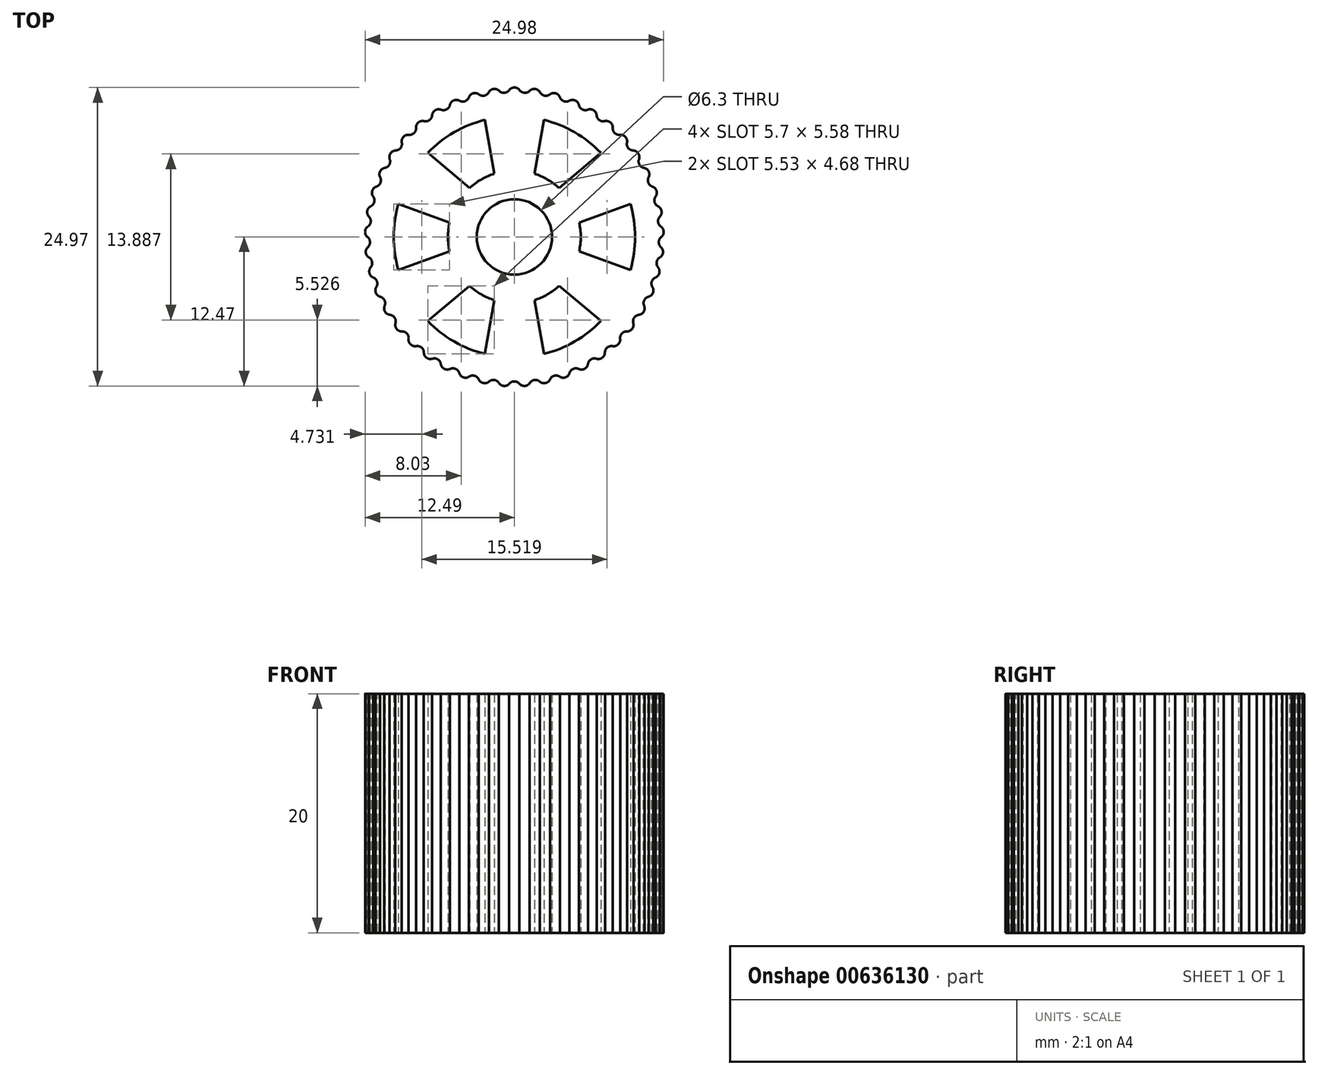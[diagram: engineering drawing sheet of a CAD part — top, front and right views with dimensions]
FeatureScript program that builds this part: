
annotation { "Feature Type Name" : "Feature", "Feature Type Description" : "" }
export const myFeature = defineFeature(function(context is Context, id is Id, definition is map)
    precondition{}
    {
        {
            var Q0;
            Q0=qCreatedBy(makeId("Top.planeOp"),FACE);
            var sketch = newSketch(context, id + "F0", { "sketchPlane" : qUnion([Q0])});
            skCircle(sketch, "E0", {"center": v(0, 0) * mm, "radius": 12.5 * mm});
            skCircle(sketch, "E1", {"center": v(0, 0) * mm, "radius": 3.15 * mm});
            skCircle(sketch, "E2", {"center": v(0, 0) * mm, "radius": 5.55 * mm});
            skCircle(sketch, "E3", {"center": v(0, 0) * mm, "radius": 10.1 * mm});
            skLineSegment(sketch, "E4", {"start": v(-5.42, -1.2) * mm, "end": v(-9.71, -2.76) * mm});
            skLineSegment(sketch, "E5", {"start": v(-5.55, 0) * mm, "end": v(-10.1, 0) * mm, "construction": true});
            skLineSegment(sketch, "E6.MirrorCS", {"start": v(-5.42, 1.2) * mm, "end": v(-9.71, 2.76) * mm});
            skLineSegment(sketch, "E7.1.0", {"start": v(-3.75, -4.1) * mm, "end": v(-7.25, -7.03) * mm});
            skLineSegment(sketch, "E7.1.1", {"start": v(-1.67, -5.3) * mm, "end": v(-2.46, -9.8) * mm});
            skLineSegment(sketch, "E7.2.0", {"start": v(1.67, -5.3) * mm, "end": v(2.46, -9.8) * mm});
            skLineSegment(sketch, "E7.2.1", {"start": v(3.75, -4.1) * mm, "end": v(7.25, -7.03) * mm});
            skLineSegment(sketch, "E7.3.0", {"start": v(5.42, -1.2) * mm, "end": v(9.71, -2.76) * mm});
            skLineSegment(sketch, "E7.3.1", {"start": v(5.42, 1.2) * mm, "end": v(9.71, 2.76) * mm});
            skLineSegment(sketch, "E7.4.0", {"start": v(3.75, 4.1) * mm, "end": v(7.25, 7.03) * mm});
            skLineSegment(sketch, "E7.4.1", {"start": v(1.67, 5.3) * mm, "end": v(2.46, 9.8) * mm});
            skLineSegment(sketch, "E7.5.0", {"start": v(-1.67, 5.3) * mm, "end": v(-2.46, 9.8) * mm});
            skLineSegment(sketch, "E7.5.1", {"start": v(-3.75, 4.1) * mm, "end": v(-7.25, 7.03) * mm});
            skSolve(sketch);
        }
        {
            var Q0;
            Q0=makeQuery(id+"F0.imprint","IMPRINT",FACE,{"disambiguationData":[TD([[makeQuery(id+"F0.imprint","IMPRINT",EDGE,{"derivedFrom":sQuery(id+"F0.wireOp",EDGE,"E0")}),1.0]])]});
            var Q1;
            {var subQ0=sQuery(id+"F0.wireOp",EDGE,"E6.MirrorCS");Q1=makeQuery(id+"F0.imprint","IMPRINT",FACE,{"disambiguationData":[TD([[makeQuery(id+"F0.imprint","IMPRINT",EDGE,{"derivedFrom":subQ0}),-1.0]])]});}
            var Q2;
            {var subQ0=sQuery(id+"F0.wireOp",EDGE,"E7.4.1");Q2=makeQuery(id+"F0.imprint","IMPRINT",FACE,{"disambiguationData":[TD([[makeQuery(id+"F0.imprint","IMPRINT",EDGE,{"derivedFrom":subQ0}),1.0]])]});}
            var Q3;
            {var subQ0=sQuery(id+"F0.wireOp",EDGE,"E7.3.1");Q3=makeQuery(id+"F0.imprint","IMPRINT",FACE,{"disambiguationData":[TD([[makeQuery(id+"F0.imprint","IMPRINT",EDGE,{"derivedFrom":subQ0}),1.0]])]});}
            var Q4;
            {var subQ0=sQuery(id+"F0.wireOp",EDGE,"E7.2.1");Q4=makeQuery(id+"F0.imprint","IMPRINT",FACE,{"disambiguationData":[TD([[makeQuery(id+"F0.imprint","IMPRINT",EDGE,{"derivedFrom":subQ0}),1.0]])]});}
            var Q5;
            {var subQ0=sQuery(id+"F0.wireOp",EDGE,"E7.1.1");Q5=makeQuery(id+"F0.imprint","IMPRINT",FACE,{"disambiguationData":[TD([[makeQuery(id+"F0.imprint","IMPRINT",EDGE,{"derivedFrom":subQ0}),1.0]])]});}
            var Q6;
            {var subQ0=sQuery(id+"F0.wireOp",EDGE,"E4");Q6=makeQuery(id+"F0.imprint","IMPRINT",FACE,{"disambiguationData":[TD([[makeQuery(id+"F0.imprint","IMPRINT",EDGE,{"derivedFrom":subQ0}),1.0]])]});}
            var Q7;
            Q7=makeQuery(id+"F0.imprint","IMPRINT",FACE,{"disambiguationData":[TD([[makeQuery(id+"F0.imprint","IMPRINT",EDGE,{"derivedFrom":sQuery(id+"F0.wireOp",EDGE,"E1")}),-1.0]])]});
            extrude(context, id + "F1", {"entities" : qUnion([Q0, Q1, Q2, Q3, Q4, Q5, Q6, Q7]), "depth" : 20 * mm, "offsetDistance" : 25 * mm});
        }
        {
            var Q0;
            Q0=makeQuery(id+"F1.opExtrude","CAP_FACE",FACE,{"disambiguationData":[OSD([sQuery(id+"F0.wireOp",EDGE,"E0"),sQuery(id+"F0.wireOp",EDGE,"E1"),sQuery(id+"F0.wireOp",EDGE,"E2"),sQuery(id+"F0.wireOp",EDGE,"E3"),sQuery(id+"F0.wireOp",EDGE,"E4"),sQuery(id+"F0.wireOp",EDGE,"E6.MirrorCS"),sQuery(id+"F0.wireOp",EDGE,"E7.1.0"),sQuery(id+"F0.wireOp",EDGE,"E7.1.1"),sQuery(id+"F0.wireOp",EDGE,"E7.2.0"),sQuery(id+"F0.wireOp",EDGE,"E7.2.1"),sQuery(id+"F0.wireOp",EDGE,"E7.3.0"),sQuery(id+"F0.wireOp",EDGE,"E7.3.1"),sQuery(id+"F0.wireOp",EDGE,"E7.4.0"),sQuery(id+"F0.wireOp",EDGE,"E7.4.1"),sQuery(id+"F0.wireOp",EDGE,"E7.5.0"),sQuery(id+"F0.wireOp",EDGE,"E7.5.1")])],"isStart":false});
            var sketch = newSketch(context, id + "F2", { "sketchPlane" : qUnion([Q0])});
            skCircle(sketch, "E8", {"center": v(0, 0) * mm, "radius": 12.3 * mm});
            skArc(sketch, "E9", {"start": v(0.43, 12.3) * mm, "mid": v(0, 12.5) * mm, "end": v(-0.43, 12.3) * mm});
            skArc(sketch, "E10", {"start": v(0.43, 12.3) * mm, "mid": v(0.84, 12.06) * mm, "end": v(1.29, 12.23) * mm});
            skLineSegment(sketch, "E11", {"start": v(-0.43, 12.3) * mm, "end": v(0.43, 12.3) * mm, "construction": true});
            skLineSegment(sketch, "E12", {"start": v(0.43, 12.3) * mm, "end": v(1.29, 12.23) * mm, "construction": true});
            skArc(sketch, "E13.1.0", {"start": v(-1.29, 12.23) * mm, "mid": v(-1.74, 12.38) * mm, "end": v(-2.14, 12.11) * mm});
            skArc(sketch, "E13.1.1", {"start": v(-1.29, 12.23) * mm, "mid": v(-0.84, 12.06) * mm, "end": v(-0.43, 12.3) * mm});
            skArc(sketch, "E13.2.0", {"start": v(-2.98, 11.93) * mm, "mid": v(-3.45, 12.02) * mm, "end": v(-3.8, 11.7) * mm});
            skArc(sketch, "E13.2.1", {"start": v(-2.98, 11.93) * mm, "mid": v(-2.51, 11.82) * mm, "end": v(-2.14, 12.11) * mm});
            skArc(sketch, "E13.3.0", {"start": v(-4.6, 11.4) * mm, "mid": v(-5.08, 11.42) * mm, "end": v(-5.4, 11.06) * mm});
            skArc(sketch, "E13.3.1", {"start": v(-4.6, 11.4) * mm, "mid": v(-4.13, 11.36) * mm, "end": v(-3.8, 11.7) * mm});
            skArc(sketch, "E13.4.0", {"start": v(-6.15, 10.65) * mm, "mid": v(-6.62, 10.6) * mm, "end": v(-6.88, 10.2) * mm});
            skArc(sketch, "E13.4.1", {"start": v(-6.15, 10.65) * mm, "mid": v(-5.67, 10.67) * mm, "end": v(-5.4, 11.06) * mm});
            skArc(sketch, "E13.5.0", {"start": v(-7.57, 9.7) * mm, "mid": v(-8.03, 9.58) * mm, "end": v(-8.23, 9.14) * mm});
            skArc(sketch, "E13.5.1", {"start": v(-7.57, 9.7) * mm, "mid": v(-7.1, 9.78) * mm, "end": v(-6.88, 10.2) * mm});
            skArc(sketch, "E13.6.0", {"start": v(-8.85, 8.54) * mm, "mid": v(-9.29, 8.36) * mm, "end": v(-9.42, 7.9) * mm});
            skArc(sketch, "E13.6.1", {"start": v(-8.85, 8.54) * mm, "mid": v(-8.4, 8.7) * mm, "end": v(-8.23, 9.14) * mm});
            skArc(sketch, "E13.7.0", {"start": v(-9.95, 7.23) * mm, "mid": v(-10.36, 6.99) * mm, "end": v(-10.43, 6.52) * mm});
            skArc(sketch, "E13.7.1", {"start": v(-9.95, 7.23) * mm, "mid": v(-9.52, 7.44) * mm, "end": v(-9.42, 7.9) * mm});
            skArc(sketch, "E13.8.0", {"start": v(-10.86, 5.77) * mm, "mid": v(-11.23, 5.48) * mm, "end": v(-11.24, 5) * mm});
            skArc(sketch, "E13.8.1", {"start": v(-10.86, 5.77) * mm, "mid": v(-10.47, 6.04) * mm, "end": v(-10.43, 6.52) * mm});
            skArc(sketch, "E13.9.0", {"start": v(-11.56, 4.2) * mm, "mid": v(-11.89, 3.86) * mm, "end": v(-11.82, 3.4) * mm});
            skArc(sketch, "E13.9.1", {"start": v(-11.56, 4.2) * mm, "mid": v(-11.2, 4.53) * mm, "end": v(-11.24, 5) * mm});
            skArc(sketch, "E13.10.0", {"start": v(-12.03, 2.56) * mm, "mid": v(-12.31, 2.17) * mm, "end": v(-12.18, 1.71) * mm});
            skArc(sketch, "E13.10.1", {"start": v(-12.03, 2.56) * mm, "mid": v(-11.73, 2.92) * mm, "end": v(-11.82, 3.4) * mm});
            skArc(sketch, "E13.11.0", {"start": v(-12.27, 0.86) * mm, "mid": v(-12.5, 0.44) * mm, "end": v(-12.3, 0) * mm});
            skArc(sketch, "E13.11.1", {"start": v(-12.27, 0.86) * mm, "mid": v(-12.02, 1.26) * mm, "end": v(-12.18, 1.71) * mm});
            skArc(sketch, "E13.12.0", {"start": v(-12.27, -0.86) * mm, "mid": v(-12.43, -1.3) * mm, "end": v(-12.18, -1.71) * mm});
            skArc(sketch, "E13.12.1", {"start": v(-12.27, -0.86) * mm, "mid": v(-12.08, -0.42) * mm, "end": v(-12.3, 0) * mm});
            skArc(sketch, "E13.13.0", {"start": v(-12.03, -2.56) * mm, "mid": v(-12.13, -3.02) * mm, "end": v(-11.82, -3.4) * mm});
            skArc(sketch, "E13.13.1", {"start": v(-12.03, -2.56) * mm, "mid": v(-11.9, -2.1) * mm, "end": v(-12.18, -1.71) * mm});
            skArc(sketch, "E13.14.0", {"start": v(-11.56, -4.2) * mm, "mid": v(-11.59, -4.68) * mm, "end": v(-11.24, -5) * mm});
            skArc(sketch, "E13.14.1", {"start": v(-11.56, -4.2) * mm, "mid": v(-11.5, -3.73) * mm, "end": v(-11.82, -3.4) * mm});
            skArc(sketch, "E13.15.0", {"start": v(-10.86, -5.77) * mm, "mid": v(-10.83, -6.25) * mm, "end": v(-10.43, -6.52) * mm});
            skArc(sketch, "E13.15.1", {"start": v(-10.86, -5.77) * mm, "mid": v(-10.86, -5.3) * mm, "end": v(-11.24, -5) * mm});
            skArc(sketch, "E13.16.0", {"start": v(-9.95, -7.23) * mm, "mid": v(-9.85, -7.7) * mm, "end": v(-9.42, -7.9) * mm});
            skArc(sketch, "E13.16.1", {"start": v(-9.95, -7.23) * mm, "mid": v(-10.02, -6.76) * mm, "end": v(-10.43, -6.52) * mm});
            skArc(sketch, "E13.17.0", {"start": v(-8.85, -8.54) * mm, "mid": v(-8.68, -9) * mm, "end": v(-8.23, -9.14) * mm});
            skArc(sketch, "E13.17.1", {"start": v(-8.85, -8.54) * mm, "mid": v(-8.98, -8.09) * mm, "end": v(-9.42, -7.9) * mm});
            skArc(sketch, "E13.18.0", {"start": v(-7.57, -9.7) * mm, "mid": v(-7.35, -10.11) * mm, "end": v(-6.88, -10.2) * mm});
            skArc(sketch, "E13.18.1", {"start": v(-7.57, -9.7) * mm, "mid": v(-7.77, -9.26) * mm, "end": v(-8.23, -9.14) * mm});
            skArc(sketch, "E13.19.0", {"start": v(-6.15, -10.65) * mm, "mid": v(-5.87, -11.04) * mm, "end": v(-5.4, -11.06) * mm});
            skArc(sketch, "E13.19.1", {"start": v(-6.15, -10.65) * mm, "mid": v(-6.4, -10.25) * mm, "end": v(-6.88, -10.2) * mm});
            skArc(sketch, "E13.20.0", {"start": v(-4.6, -11.4) * mm, "mid": v(-4.28, -11.75) * mm, "end": v(-3.8, -11.7) * mm});
            skArc(sketch, "E13.20.1", {"start": v(-4.6, -11.4) * mm, "mid": v(-4.92, -11.04) * mm, "end": v(-5.4, -11.06) * mm});
            skArc(sketch, "E13.21.0", {"start": v(-2.98, -11.93) * mm, "mid": v(-2.6, -12.23) * mm, "end": v(-2.14, -12.11) * mm});
            skArc(sketch, "E13.21.1", {"start": v(-2.98, -11.93) * mm, "mid": v(-3.33, -11.62) * mm, "end": v(-3.8, -11.7) * mm});
            skArc(sketch, "E13.22.0", {"start": v(-1.29, -12.23) * mm, "mid": v(-0.87, -12.47) * mm, "end": v(-0.43, -12.3) * mm});
            skArc(sketch, "E13.22.1", {"start": v(-1.29, -12.23) * mm, "mid": v(-1.68, -11.97) * mm, "end": v(-2.14, -12.11) * mm});
            skArc(sketch, "E13.23.0", {"start": v(0.43, -12.3) * mm, "mid": v(0.87, -12.47) * mm, "end": v(1.29, -12.23) * mm});
            skArc(sketch, "E13.23.1", {"start": v(0.43, -12.3) * mm, "mid": v(0, -12.09) * mm, "end": v(-0.43, -12.3) * mm});
            skArc(sketch, "E13.24.0", {"start": v(2.14, -12.11) * mm, "mid": v(2.6, -12.23) * mm, "end": v(2.98, -11.93) * mm});
            skArc(sketch, "E13.24.1", {"start": v(2.14, -12.11) * mm, "mid": v(1.68, -11.97) * mm, "end": v(1.29, -12.23) * mm});
            skArc(sketch, "E13.25.0", {"start": v(3.8, -11.7) * mm, "mid": v(4.28, -11.75) * mm, "end": v(4.6, -11.4) * mm});
            skArc(sketch, "E13.25.1", {"start": v(3.8, -11.7) * mm, "mid": v(3.33, -11.62) * mm, "end": v(2.98, -11.93) * mm});
            skArc(sketch, "E13.26.0", {"start": v(5.4, -11.06) * mm, "mid": v(5.87, -11.04) * mm, "end": v(6.15, -10.65) * mm});
            skArc(sketch, "E13.26.1", {"start": v(5.4, -11.06) * mm, "mid": v(4.92, -11.04) * mm, "end": v(4.6, -11.4) * mm});
            skArc(sketch, "E13.27.0", {"start": v(6.88, -10.2) * mm, "mid": v(7.35, -10.11) * mm, "end": v(7.57, -9.7) * mm});
            skArc(sketch, "E13.27.1", {"start": v(6.88, -10.2) * mm, "mid": v(6.4, -10.25) * mm, "end": v(6.15, -10.65) * mm});
            skArc(sketch, "E13.28.0", {"start": v(8.23, -9.14) * mm, "mid": v(8.68, -9) * mm, "end": v(8.85, -8.54) * mm});
            skArc(sketch, "E13.28.1", {"start": v(8.23, -9.14) * mm, "mid": v(7.77, -9.26) * mm, "end": v(7.57, -9.7) * mm});
            skArc(sketch, "E13.29.0", {"start": v(9.42, -7.9) * mm, "mid": v(9.85, -7.7) * mm, "end": v(9.95, -7.23) * mm});
            skArc(sketch, "E13.29.1", {"start": v(9.42, -7.9) * mm, "mid": v(8.98, -8.09) * mm, "end": v(8.85, -8.54) * mm});
            skArc(sketch, "E13.30.0", {"start": v(10.43, -6.52) * mm, "mid": v(10.83, -6.25) * mm, "end": v(10.86, -5.77) * mm});
            skArc(sketch, "E13.30.1", {"start": v(10.43, -6.52) * mm, "mid": v(10.02, -6.76) * mm, "end": v(9.95, -7.23) * mm});
            skArc(sketch, "E13.31.0", {"start": v(11.24, -5) * mm, "mid": v(11.59, -4.68) * mm, "end": v(11.56, -4.2) * mm});
            skArc(sketch, "E13.31.1", {"start": v(11.24, -5) * mm, "mid": v(10.86, -5.3) * mm, "end": v(10.86, -5.77) * mm});
            skArc(sketch, "E13.32.0", {"start": v(11.82, -3.4) * mm, "mid": v(12.13, -3.02) * mm, "end": v(12.03, -2.56) * mm});
            skArc(sketch, "E13.32.1", {"start": v(11.82, -3.4) * mm, "mid": v(11.5, -3.73) * mm, "end": v(11.56, -4.2) * mm});
            skArc(sketch, "E13.33.0", {"start": v(12.18, -1.71) * mm, "mid": v(12.43, -1.3) * mm, "end": v(12.27, -0.86) * mm});
            skArc(sketch, "E13.33.1", {"start": v(12.18, -1.71) * mm, "mid": v(11.9, -2.1) * mm, "end": v(12.03, -2.56) * mm});
            skArc(sketch, "E13.34.0", {"start": v(12.3, 0) * mm, "mid": v(12.5, 0.44) * mm, "end": v(12.27, 0.86) * mm});
            skArc(sketch, "E13.34.1", {"start": v(12.3, 0) * mm, "mid": v(12.08, -0.42) * mm, "end": v(12.27, -0.86) * mm});
            skArc(sketch, "E13.35.0", {"start": v(12.18, 1.71) * mm, "mid": v(12.31, 2.17) * mm, "end": v(12.03, 2.56) * mm});
            skArc(sketch, "E13.35.1", {"start": v(12.18, 1.71) * mm, "mid": v(12.02, 1.26) * mm, "end": v(12.27, 0.86) * mm});
            skArc(sketch, "E13.36.0", {"start": v(11.82, 3.4) * mm, "mid": v(11.89, 3.86) * mm, "end": v(11.56, 4.2) * mm});
            skArc(sketch, "E13.36.1", {"start": v(11.82, 3.4) * mm, "mid": v(11.73, 2.92) * mm, "end": v(12.03, 2.56) * mm});
            skArc(sketch, "E13.37.0", {"start": v(11.24, 5) * mm, "mid": v(11.23, 5.48) * mm, "end": v(10.86, 5.77) * mm});
            skArc(sketch, "E13.37.1", {"start": v(11.24, 5) * mm, "mid": v(11.2, 4.53) * mm, "end": v(11.56, 4.2) * mm});
            skArc(sketch, "E13.38.0", {"start": v(10.43, 6.52) * mm, "mid": v(10.36, 6.99) * mm, "end": v(9.95, 7.23) * mm});
            skArc(sketch, "E13.38.1", {"start": v(10.43, 6.52) * mm, "mid": v(10.47, 6.04) * mm, "end": v(10.86, 5.77) * mm});
            skArc(sketch, "E13.39.0", {"start": v(9.42, 7.9) * mm, "mid": v(9.29, 8.36) * mm, "end": v(8.85, 8.54) * mm});
            skArc(sketch, "E13.39.1", {"start": v(9.42, 7.9) * mm, "mid": v(9.52, 7.44) * mm, "end": v(9.95, 7.23) * mm});
            skArc(sketch, "E13.40.0", {"start": v(8.23, 9.14) * mm, "mid": v(8.03, 9.58) * mm, "end": v(7.57, 9.7) * mm});
            skArc(sketch, "E13.40.1", {"start": v(8.23, 9.14) * mm, "mid": v(8.4, 8.7) * mm, "end": v(8.85, 8.54) * mm});
            skArc(sketch, "E13.41.0", {"start": v(6.88, 10.2) * mm, "mid": v(6.62, 10.6) * mm, "end": v(6.15, 10.65) * mm});
            skArc(sketch, "E13.41.1", {"start": v(6.88, 10.2) * mm, "mid": v(7.1, 9.78) * mm, "end": v(7.57, 9.7) * mm});
            skArc(sketch, "E13.42.0", {"start": v(5.4, 11.06) * mm, "mid": v(5.08, 11.42) * mm, "end": v(4.6, 11.4) * mm});
            skArc(sketch, "E13.42.1", {"start": v(5.4, 11.06) * mm, "mid": v(5.67, 10.67) * mm, "end": v(6.15, 10.65) * mm});
            skArc(sketch, "E13.43.0", {"start": v(3.8, 11.7) * mm, "mid": v(3.45, 12.02) * mm, "end": v(2.98, 11.93) * mm});
            skArc(sketch, "E13.43.1", {"start": v(3.8, 11.7) * mm, "mid": v(4.13, 11.36) * mm, "end": v(4.6, 11.4) * mm});
            skArc(sketch, "E13.44.0", {"start": v(2.14, 12.11) * mm, "mid": v(1.74, 12.38) * mm, "end": v(1.29, 12.23) * mm});
            skArc(sketch, "E13.44.1", {"start": v(2.14, 12.11) * mm, "mid": v(2.51, 11.82) * mm, "end": v(2.98, 11.93) * mm});
            skSolve(sketch);
        }
        {
            var Q0;
            {var subQ37=sQuery(id+"F2.wireOp",EDGE,"E10");Q0=makeQuery(id+"F2.imprint","IMPRINT",FACE,{"disambiguationData":[TD([[makeQuery(id+"F2.imprint","IMPRINT",EDGE,{"derivedFrom":subQ37}),-1.0]])]});}
            var Q1;
            {var subQ0=sQuery(id+"F2.wireOp",EDGE,"E13.22.0");var subQ1=sQuery(id+"F2.wireOp",EDGE,"E8");var subQ4=makeQuery(id+"F2.imprint","INTERSECT",VERTEX,{"derivedFrom":[subQ1,subQ0]});Q1=makeQuery(id+"F2.imprint","IMPRINT",FACE,{"disambiguationData":[TD([[makeQuery(id+"F2.imprint","IMPRINT",EDGE,{"disambiguationData":[TD([[subQ4,1.0]])],"derivedFrom":subQ1}),-1.0]])]});}
            var Q2;
            {var subQ0=sQuery(id+"F2.wireOp",EDGE,"E13.23.0");var subQ1=sQuery(id+"F2.wireOp",EDGE,"E8");var subQ4=makeQuery(id+"F2.imprint","INTERSECT",VERTEX,{"derivedFrom":[subQ1,subQ0]});Q2=makeQuery(id+"F2.imprint","IMPRINT",FACE,{"disambiguationData":[TD([[makeQuery(id+"F2.imprint","IMPRINT",EDGE,{"disambiguationData":[TD([[subQ4,1.0]])],"derivedFrom":subQ1}),-1.0]])]});}
            var Q3;
            {var subQ0=sQuery(id+"F2.wireOp",EDGE,"E13.24.0");var subQ1=sQuery(id+"F2.wireOp",EDGE,"E8");var subQ4=makeQuery(id+"F2.imprint","INTERSECT",VERTEX,{"derivedFrom":[subQ1,subQ0]});Q3=makeQuery(id+"F2.imprint","IMPRINT",FACE,{"disambiguationData":[TD([[makeQuery(id+"F2.imprint","IMPRINT",EDGE,{"disambiguationData":[TD([[subQ4,1.0]])],"derivedFrom":subQ1}),-1.0]])]});}
            var Q4;
            {var subQ0=sQuery(id+"F2.wireOp",EDGE,"E13.25.0");var subQ1=sQuery(id+"F2.wireOp",EDGE,"E8");var subQ4=makeQuery(id+"F2.imprint","INTERSECT",VERTEX,{"derivedFrom":[subQ1,subQ0]});Q4=makeQuery(id+"F2.imprint","IMPRINT",FACE,{"disambiguationData":[TD([[makeQuery(id+"F2.imprint","IMPRINT",EDGE,{"disambiguationData":[TD([[subQ4,1.0]])],"derivedFrom":subQ1}),-1.0]])]});}
            var Q5;
            {var subQ0=sQuery(id+"F2.wireOp",EDGE,"E13.26.0");var subQ1=sQuery(id+"F2.wireOp",EDGE,"E8");var subQ4=makeQuery(id+"F2.imprint","INTERSECT",VERTEX,{"derivedFrom":[subQ1,subQ0]});Q5=makeQuery(id+"F2.imprint","IMPRINT",FACE,{"disambiguationData":[TD([[makeQuery(id+"F2.imprint","IMPRINT",EDGE,{"disambiguationData":[TD([[subQ4,1.0]])],"derivedFrom":subQ1}),-1.0]])]});}
            var Q6;
            {var subQ0=sQuery(id+"F2.wireOp",EDGE,"E13.27.0");var subQ1=sQuery(id+"F2.wireOp",EDGE,"E8");var subQ4=makeQuery(id+"F2.imprint","INTERSECT",VERTEX,{"derivedFrom":[subQ1,subQ0]});Q6=makeQuery(id+"F2.imprint","IMPRINT",FACE,{"disambiguationData":[TD([[makeQuery(id+"F2.imprint","IMPRINT",EDGE,{"disambiguationData":[TD([[subQ4,1.0]])],"derivedFrom":subQ1}),-1.0]])]});}
            var Q7;
            {var subQ0=sQuery(id+"F2.wireOp",EDGE,"E13.28.0");var subQ1=sQuery(id+"F2.wireOp",EDGE,"E8");var subQ4=makeQuery(id+"F2.imprint","INTERSECT",VERTEX,{"derivedFrom":[subQ1,subQ0]});Q7=makeQuery(id+"F2.imprint","IMPRINT",FACE,{"disambiguationData":[TD([[makeQuery(id+"F2.imprint","IMPRINT",EDGE,{"disambiguationData":[TD([[subQ4,1.0]])],"derivedFrom":subQ1}),-1.0]])]});}
            var Q8;
            {var subQ0=sQuery(id+"F2.wireOp",EDGE,"E13.29.0");var subQ1=sQuery(id+"F2.wireOp",EDGE,"E8");var subQ4=makeQuery(id+"F2.imprint","INTERSECT",VERTEX,{"derivedFrom":[subQ1,subQ0]});Q8=makeQuery(id+"F2.imprint","IMPRINT",FACE,{"disambiguationData":[TD([[makeQuery(id+"F2.imprint","IMPRINT",EDGE,{"disambiguationData":[TD([[subQ4,1.0]])],"derivedFrom":subQ1}),-1.0]])]});}
            var Q9;
            {var subQ0=sQuery(id+"F2.wireOp",EDGE,"E13.30.0");var subQ1=sQuery(id+"F2.wireOp",EDGE,"E8");var subQ4=makeQuery(id+"F2.imprint","INTERSECT",VERTEX,{"derivedFrom":[subQ1,subQ0]});Q9=makeQuery(id+"F2.imprint","IMPRINT",FACE,{"disambiguationData":[TD([[makeQuery(id+"F2.imprint","IMPRINT",EDGE,{"disambiguationData":[TD([[subQ4,1.0]])],"derivedFrom":subQ1}),-1.0]])]});}
            var Q10;
            {var subQ0=sQuery(id+"F2.wireOp",EDGE,"E13.31.0");var subQ1=sQuery(id+"F2.wireOp",EDGE,"E8");var subQ4=makeQuery(id+"F2.imprint","INTERSECT",VERTEX,{"derivedFrom":[subQ1,subQ0]});Q10=makeQuery(id+"F2.imprint","IMPRINT",FACE,{"disambiguationData":[TD([[makeQuery(id+"F2.imprint","IMPRINT",EDGE,{"disambiguationData":[TD([[subQ4,1.0]])],"derivedFrom":subQ1}),-1.0]])]});}
            var Q11;
            {var subQ0=sQuery(id+"F2.wireOp",EDGE,"E13.32.0");var subQ1=sQuery(id+"F2.wireOp",EDGE,"E8");var subQ4=makeQuery(id+"F2.imprint","INTERSECT",VERTEX,{"derivedFrom":[subQ1,subQ0]});Q11=makeQuery(id+"F2.imprint","IMPRINT",FACE,{"disambiguationData":[TD([[makeQuery(id+"F2.imprint","IMPRINT",EDGE,{"disambiguationData":[TD([[subQ4,1.0]])],"derivedFrom":subQ1}),-1.0]])]});}
            var Q12;
            {var subQ0=sQuery(id+"F2.wireOp",EDGE,"E13.33.0");var subQ1=sQuery(id+"F2.wireOp",EDGE,"E8");var subQ4=makeQuery(id+"F2.imprint","INTERSECT",VERTEX,{"derivedFrom":[subQ1,subQ0]});Q12=makeQuery(id+"F2.imprint","IMPRINT",FACE,{"disambiguationData":[TD([[makeQuery(id+"F2.imprint","IMPRINT",EDGE,{"disambiguationData":[TD([[subQ4,1.0]])],"derivedFrom":subQ1}),-1.0]])]});}
            var Q13;
            {var subQ0=sQuery(id+"F2.wireOp",EDGE,"E13.34.0");var subQ1=sQuery(id+"F2.wireOp",EDGE,"E8");var subQ4=makeQuery(id+"F2.imprint","INTERSECT",VERTEX,{"derivedFrom":[subQ1,subQ0]});Q13=makeQuery(id+"F2.imprint","IMPRINT",FACE,{"disambiguationData":[TD([[makeQuery(id+"F2.imprint","IMPRINT",EDGE,{"disambiguationData":[TD([[subQ4,1.0]])],"derivedFrom":subQ1}),-1.0]])]});}
            var Q14;
            {var subQ0=sQuery(id+"F2.wireOp",EDGE,"E13.35.0");var subQ1=sQuery(id+"F2.wireOp",EDGE,"E8");var subQ4=makeQuery(id+"F2.imprint","INTERSECT",VERTEX,{"derivedFrom":[subQ1,subQ0]});Q14=makeQuery(id+"F2.imprint","IMPRINT",FACE,{"disambiguationData":[TD([[makeQuery(id+"F2.imprint","IMPRINT",EDGE,{"disambiguationData":[TD([[subQ4,1.0]])],"derivedFrom":subQ1}),-1.0]])]});}
            var Q15;
            {var subQ0=sQuery(id+"F2.wireOp",EDGE,"E13.36.0");var subQ1=sQuery(id+"F2.wireOp",EDGE,"E8");var subQ4=makeQuery(id+"F2.imprint","INTERSECT",VERTEX,{"derivedFrom":[subQ1,subQ0]});Q15=makeQuery(id+"F2.imprint","IMPRINT",FACE,{"disambiguationData":[TD([[makeQuery(id+"F2.imprint","IMPRINT",EDGE,{"disambiguationData":[TD([[subQ4,1.0]])],"derivedFrom":subQ1}),-1.0]])]});}
            var Q16;
            {var subQ0=sQuery(id+"F2.wireOp",EDGE,"E13.37.0");var subQ1=sQuery(id+"F2.wireOp",EDGE,"E8");var subQ4=makeQuery(id+"F2.imprint","INTERSECT",VERTEX,{"derivedFrom":[subQ1,subQ0]});Q16=makeQuery(id+"F2.imprint","IMPRINT",FACE,{"disambiguationData":[TD([[makeQuery(id+"F2.imprint","IMPRINT",EDGE,{"disambiguationData":[TD([[subQ4,1.0]])],"derivedFrom":subQ1}),-1.0]])]});}
            var Q17;
            {var subQ0=sQuery(id+"F2.wireOp",EDGE,"E13.38.0");var subQ1=sQuery(id+"F2.wireOp",EDGE,"E8");var subQ4=makeQuery(id+"F2.imprint","INTERSECT",VERTEX,{"derivedFrom":[subQ1,subQ0]});Q17=makeQuery(id+"F2.imprint","IMPRINT",FACE,{"disambiguationData":[TD([[makeQuery(id+"F2.imprint","IMPRINT",EDGE,{"disambiguationData":[TD([[subQ4,1.0]])],"derivedFrom":subQ1}),-1.0]])]});}
            var Q18;
            {var subQ0=sQuery(id+"F2.wireOp",EDGE,"E13.39.0");var subQ1=sQuery(id+"F2.wireOp",EDGE,"E8");var subQ4=makeQuery(id+"F2.imprint","INTERSECT",VERTEX,{"derivedFrom":[subQ1,subQ0]});Q18=makeQuery(id+"F2.imprint","IMPRINT",FACE,{"disambiguationData":[TD([[makeQuery(id+"F2.imprint","IMPRINT",EDGE,{"disambiguationData":[TD([[subQ4,1.0]])],"derivedFrom":subQ1}),-1.0]])]});}
            var Q19;
            {var subQ0=sQuery(id+"F2.wireOp",EDGE,"E13.40.0");var subQ1=sQuery(id+"F2.wireOp",EDGE,"E8");var subQ4=makeQuery(id+"F2.imprint","INTERSECT",VERTEX,{"derivedFrom":[subQ1,subQ0]});Q19=makeQuery(id+"F2.imprint","IMPRINT",FACE,{"disambiguationData":[TD([[makeQuery(id+"F2.imprint","IMPRINT",EDGE,{"disambiguationData":[TD([[subQ4,1.0]])],"derivedFrom":subQ1}),-1.0]])]});}
            var Q20;
            {var subQ0=sQuery(id+"F2.wireOp",EDGE,"E13.41.0");var subQ1=sQuery(id+"F2.wireOp",EDGE,"E8");var subQ4=makeQuery(id+"F2.imprint","INTERSECT",VERTEX,{"derivedFrom":[subQ1,subQ0]});Q20=makeQuery(id+"F2.imprint","IMPRINT",FACE,{"disambiguationData":[TD([[makeQuery(id+"F2.imprint","IMPRINT",EDGE,{"disambiguationData":[TD([[subQ4,1.0]])],"derivedFrom":subQ1}),-1.0]])]});}
            var Q21;
            {var subQ0=sQuery(id+"F2.wireOp",EDGE,"E13.42.0");var subQ1=sQuery(id+"F2.wireOp",EDGE,"E8");var subQ4=makeQuery(id+"F2.imprint","INTERSECT",VERTEX,{"derivedFrom":[subQ1,subQ0]});Q21=makeQuery(id+"F2.imprint","IMPRINT",FACE,{"disambiguationData":[TD([[makeQuery(id+"F2.imprint","IMPRINT",EDGE,{"disambiguationData":[TD([[subQ4,1.0]])],"derivedFrom":subQ1}),-1.0]])]});}
            var Q22;
            {var subQ0=sQuery(id+"F2.wireOp",EDGE,"E13.43.0");var subQ1=sQuery(id+"F2.wireOp",EDGE,"E8");var subQ4=makeQuery(id+"F2.imprint","INTERSECT",VERTEX,{"derivedFrom":[subQ1,subQ0]});Q22=makeQuery(id+"F2.imprint","IMPRINT",FACE,{"disambiguationData":[TD([[makeQuery(id+"F2.imprint","IMPRINT",EDGE,{"disambiguationData":[TD([[subQ4,1.0]])],"derivedFrom":subQ1}),-1.0]])]});}
            var Q23;
            {var subQ0=sQuery(id+"F2.wireOp",EDGE,"E8");var subQ1=makeQuery(id+"F2.imprint","INTERSECT",VERTEX,{"derivedFrom":[subQ0,sQuery(id+"F2.wireOp",EDGE,"E10")]});Q23=makeQuery(id+"F2.imprint","IMPRINT",FACE,{"disambiguationData":[TD([[makeQuery(id+"F2.imprint","IMPRINT",EDGE,{"disambiguationData":[TD([[subQ1,-1.0]])],"derivedFrom":subQ0}),-1.0]])]});}
            var Q24;
            {var subQ0=sQuery(id+"F2.wireOp",EDGE,"E9");var subQ1=sQuery(id+"F2.wireOp",EDGE,"E8");var subQ4=makeQuery(id+"F2.imprint","INTERSECT",VERTEX,{"derivedFrom":[subQ1,subQ0]});Q24=makeQuery(id+"F2.imprint","IMPRINT",FACE,{"disambiguationData":[TD([[makeQuery(id+"F2.imprint","IMPRINT",EDGE,{"disambiguationData":[TD([[subQ4,1.0]])],"derivedFrom":subQ1}),-1.0]])]});}
            var Q25;
            {var subQ0=sQuery(id+"F2.wireOp",EDGE,"E13.1.0");var subQ1=sQuery(id+"F2.wireOp",EDGE,"E8");var subQ4=makeQuery(id+"F2.imprint","INTERSECT",VERTEX,{"derivedFrom":[subQ1,subQ0]});Q25=makeQuery(id+"F2.imprint","IMPRINT",FACE,{"disambiguationData":[TD([[makeQuery(id+"F2.imprint","IMPRINT",EDGE,{"disambiguationData":[TD([[subQ4,1.0]])],"derivedFrom":subQ1}),-1.0]])]});}
            var Q26;
            {var subQ0=sQuery(id+"F2.wireOp",EDGE,"E13.2.0");var subQ1=sQuery(id+"F2.wireOp",EDGE,"E8");var subQ4=makeQuery(id+"F2.imprint","INTERSECT",VERTEX,{"derivedFrom":[subQ1,subQ0]});Q26=makeQuery(id+"F2.imprint","IMPRINT",FACE,{"disambiguationData":[TD([[makeQuery(id+"F2.imprint","IMPRINT",EDGE,{"disambiguationData":[TD([[subQ4,1.0]])],"derivedFrom":subQ1}),-1.0]])]});}
            var Q27;
            {var subQ0=sQuery(id+"F2.wireOp",EDGE,"E13.3.0");var subQ1=sQuery(id+"F2.wireOp",EDGE,"E8");var subQ4=makeQuery(id+"F2.imprint","INTERSECT",VERTEX,{"derivedFrom":[subQ1,subQ0]});Q27=makeQuery(id+"F2.imprint","IMPRINT",FACE,{"disambiguationData":[TD([[makeQuery(id+"F2.imprint","IMPRINT",EDGE,{"disambiguationData":[TD([[subQ4,1.0]])],"derivedFrom":subQ1}),-1.0]])]});}
            var Q28;
            {var subQ0=sQuery(id+"F2.wireOp",EDGE,"E13.4.0");var subQ1=sQuery(id+"F2.wireOp",EDGE,"E8");var subQ4=makeQuery(id+"F2.imprint","INTERSECT",VERTEX,{"derivedFrom":[subQ1,subQ0]});Q28=makeQuery(id+"F2.imprint","IMPRINT",FACE,{"disambiguationData":[TD([[makeQuery(id+"F2.imprint","IMPRINT",EDGE,{"disambiguationData":[TD([[subQ4,1.0]])],"derivedFrom":subQ1}),-1.0]])]});}
            var Q29;
            {var subQ0=sQuery(id+"F2.wireOp",EDGE,"E13.5.0");var subQ1=sQuery(id+"F2.wireOp",EDGE,"E8");var subQ4=makeQuery(id+"F2.imprint","INTERSECT",VERTEX,{"derivedFrom":[subQ1,subQ0]});Q29=makeQuery(id+"F2.imprint","IMPRINT",FACE,{"disambiguationData":[TD([[makeQuery(id+"F2.imprint","IMPRINT",EDGE,{"disambiguationData":[TD([[subQ4,1.0]])],"derivedFrom":subQ1}),-1.0]])]});}
            var Q30;
            {var subQ0=sQuery(id+"F2.wireOp",EDGE,"E13.6.0");var subQ1=sQuery(id+"F2.wireOp",EDGE,"E8");var subQ4=makeQuery(id+"F2.imprint","INTERSECT",VERTEX,{"derivedFrom":[subQ1,subQ0]});Q30=makeQuery(id+"F2.imprint","IMPRINT",FACE,{"disambiguationData":[TD([[makeQuery(id+"F2.imprint","IMPRINT",EDGE,{"disambiguationData":[TD([[subQ4,1.0]])],"derivedFrom":subQ1}),-1.0]])]});}
            var Q31;
            {var subQ0=sQuery(id+"F2.wireOp",EDGE,"E13.7.0");var subQ1=sQuery(id+"F2.wireOp",EDGE,"E8");var subQ4=makeQuery(id+"F2.imprint","INTERSECT",VERTEX,{"derivedFrom":[subQ1,subQ0]});Q31=makeQuery(id+"F2.imprint","IMPRINT",FACE,{"disambiguationData":[TD([[makeQuery(id+"F2.imprint","IMPRINT",EDGE,{"disambiguationData":[TD([[subQ4,1.0]])],"derivedFrom":subQ1}),-1.0]])]});}
            var Q32;
            {var subQ0=sQuery(id+"F2.wireOp",EDGE,"E13.8.0");var subQ1=sQuery(id+"F2.wireOp",EDGE,"E8");var subQ4=makeQuery(id+"F2.imprint","INTERSECT",VERTEX,{"derivedFrom":[subQ1,subQ0]});Q32=makeQuery(id+"F2.imprint","IMPRINT",FACE,{"disambiguationData":[TD([[makeQuery(id+"F2.imprint","IMPRINT",EDGE,{"disambiguationData":[TD([[subQ4,1.0]])],"derivedFrom":subQ1}),-1.0]])]});}
            var Q33;
            {var subQ0=sQuery(id+"F2.wireOp",EDGE,"E13.9.0");var subQ1=sQuery(id+"F2.wireOp",EDGE,"E8");var subQ4=makeQuery(id+"F2.imprint","INTERSECT",VERTEX,{"derivedFrom":[subQ1,subQ0]});Q33=makeQuery(id+"F2.imprint","IMPRINT",FACE,{"disambiguationData":[TD([[makeQuery(id+"F2.imprint","IMPRINT",EDGE,{"disambiguationData":[TD([[subQ4,1.0]])],"derivedFrom":subQ1}),-1.0]])]});}
            var Q34;
            {var subQ0=sQuery(id+"F2.wireOp",EDGE,"E13.10.0");var subQ1=sQuery(id+"F2.wireOp",EDGE,"E8");var subQ4=makeQuery(id+"F2.imprint","INTERSECT",VERTEX,{"derivedFrom":[subQ1,subQ0]});Q34=makeQuery(id+"F2.imprint","IMPRINT",FACE,{"disambiguationData":[TD([[makeQuery(id+"F2.imprint","IMPRINT",EDGE,{"disambiguationData":[TD([[subQ4,1.0]])],"derivedFrom":subQ1}),-1.0]])]});}
            var Q35;
            {var subQ0=sQuery(id+"F2.wireOp",EDGE,"E13.11.0");var subQ1=sQuery(id+"F2.wireOp",EDGE,"E8");var subQ4=makeQuery(id+"F2.imprint","INTERSECT",VERTEX,{"derivedFrom":[subQ1,subQ0]});Q35=makeQuery(id+"F2.imprint","IMPRINT",FACE,{"disambiguationData":[TD([[makeQuery(id+"F2.imprint","IMPRINT",EDGE,{"disambiguationData":[TD([[subQ4,1.0]])],"derivedFrom":subQ1}),-1.0]])]});}
            var Q36;
            {var subQ0=sQuery(id+"F2.wireOp",EDGE,"E13.12.0");var subQ1=sQuery(id+"F2.wireOp",EDGE,"E8");var subQ4=makeQuery(id+"F2.imprint","INTERSECT",VERTEX,{"derivedFrom":[subQ1,subQ0]});Q36=makeQuery(id+"F2.imprint","IMPRINT",FACE,{"disambiguationData":[TD([[makeQuery(id+"F2.imprint","IMPRINT",EDGE,{"disambiguationData":[TD([[subQ4,1.0]])],"derivedFrom":subQ1}),-1.0]])]});}
            var Q37;
            {var subQ0=sQuery(id+"F2.wireOp",EDGE,"E13.13.0");var subQ1=sQuery(id+"F2.wireOp",EDGE,"E8");var subQ4=makeQuery(id+"F2.imprint","INTERSECT",VERTEX,{"derivedFrom":[subQ1,subQ0]});Q37=makeQuery(id+"F2.imprint","IMPRINT",FACE,{"disambiguationData":[TD([[makeQuery(id+"F2.imprint","IMPRINT",EDGE,{"disambiguationData":[TD([[subQ4,1.0]])],"derivedFrom":subQ1}),-1.0]])]});}
            var Q38;
            {var subQ0=sQuery(id+"F2.wireOp",EDGE,"E13.14.0");var subQ1=sQuery(id+"F2.wireOp",EDGE,"E8");var subQ4=makeQuery(id+"F2.imprint","INTERSECT",VERTEX,{"derivedFrom":[subQ1,subQ0]});Q38=makeQuery(id+"F2.imprint","IMPRINT",FACE,{"disambiguationData":[TD([[makeQuery(id+"F2.imprint","IMPRINT",EDGE,{"disambiguationData":[TD([[subQ4,1.0]])],"derivedFrom":subQ1}),-1.0]])]});}
            var Q39;
            {var subQ0=sQuery(id+"F2.wireOp",EDGE,"E13.15.0");var subQ1=sQuery(id+"F2.wireOp",EDGE,"E8");var subQ4=makeQuery(id+"F2.imprint","INTERSECT",VERTEX,{"derivedFrom":[subQ1,subQ0]});Q39=makeQuery(id+"F2.imprint","IMPRINT",FACE,{"disambiguationData":[TD([[makeQuery(id+"F2.imprint","IMPRINT",EDGE,{"disambiguationData":[TD([[subQ4,1.0]])],"derivedFrom":subQ1}),-1.0]])]});}
            var Q40;
            {var subQ0=sQuery(id+"F2.wireOp",EDGE,"E13.16.0");var subQ1=sQuery(id+"F2.wireOp",EDGE,"E8");var subQ4=makeQuery(id+"F2.imprint","INTERSECT",VERTEX,{"derivedFrom":[subQ1,subQ0]});Q40=makeQuery(id+"F2.imprint","IMPRINT",FACE,{"disambiguationData":[TD([[makeQuery(id+"F2.imprint","IMPRINT",EDGE,{"disambiguationData":[TD([[subQ4,1.0]])],"derivedFrom":subQ1}),-1.0]])]});}
            var Q41;
            {var subQ0=sQuery(id+"F2.wireOp",EDGE,"E13.17.0");var subQ1=sQuery(id+"F2.wireOp",EDGE,"E8");var subQ4=makeQuery(id+"F2.imprint","INTERSECT",VERTEX,{"derivedFrom":[subQ1,subQ0]});Q41=makeQuery(id+"F2.imprint","IMPRINT",FACE,{"disambiguationData":[TD([[makeQuery(id+"F2.imprint","IMPRINT",EDGE,{"disambiguationData":[TD([[subQ4,1.0]])],"derivedFrom":subQ1}),-1.0]])]});}
            var Q42;
            {var subQ0=sQuery(id+"F2.wireOp",EDGE,"E13.18.0");var subQ1=sQuery(id+"F2.wireOp",EDGE,"E8");var subQ4=makeQuery(id+"F2.imprint","INTERSECT",VERTEX,{"derivedFrom":[subQ1,subQ0]});Q42=makeQuery(id+"F2.imprint","IMPRINT",FACE,{"disambiguationData":[TD([[makeQuery(id+"F2.imprint","IMPRINT",EDGE,{"disambiguationData":[TD([[subQ4,1.0]])],"derivedFrom":subQ1}),-1.0]])]});}
            var Q43;
            {var subQ0=sQuery(id+"F2.wireOp",EDGE,"E13.19.0");var subQ1=sQuery(id+"F2.wireOp",EDGE,"E8");var subQ4=makeQuery(id+"F2.imprint","INTERSECT",VERTEX,{"derivedFrom":[subQ1,subQ0]});Q43=makeQuery(id+"F2.imprint","IMPRINT",FACE,{"disambiguationData":[TD([[makeQuery(id+"F2.imprint","IMPRINT",EDGE,{"disambiguationData":[TD([[subQ4,1.0]])],"derivedFrom":subQ1}),-1.0]])]});}
            var Q44;
            {var subQ0=sQuery(id+"F2.wireOp",EDGE,"E13.20.0");var subQ1=sQuery(id+"F2.wireOp",EDGE,"E8");var subQ4=makeQuery(id+"F2.imprint","INTERSECT",VERTEX,{"derivedFrom":[subQ1,subQ0]});Q44=makeQuery(id+"F2.imprint","IMPRINT",FACE,{"disambiguationData":[TD([[makeQuery(id+"F2.imprint","IMPRINT",EDGE,{"disambiguationData":[TD([[subQ4,1.0]])],"derivedFrom":subQ1}),-1.0]])]});}
            var Q45;
            {var subQ0=sQuery(id+"F2.wireOp",EDGE,"E13.21.0");var subQ1=sQuery(id+"F2.wireOp",EDGE,"E8");var subQ4=makeQuery(id+"F2.imprint","INTERSECT",VERTEX,{"derivedFrom":[subQ1,subQ0]});Q45=makeQuery(id+"F2.imprint","IMPRINT",FACE,{"disambiguationData":[TD([[makeQuery(id+"F2.imprint","IMPRINT",EDGE,{"disambiguationData":[TD([[subQ4,1.0]])],"derivedFrom":subQ1}),-1.0]])]});}
            extrude(context, id + "F3", {"entities" : qUnion([Q0, Q1, Q2, Q3, Q4, Q5, Q6, Q7, Q8, Q9, Q10, Q11, Q12, Q13, Q14, Q15, Q16, Q17, Q18, Q19, Q20, Q21, Q22, Q23, Q24, Q25, Q26, Q27, Q28, Q29, Q30, Q31, Q32, Q33, Q34, Q35, Q36, Q37, Q38, Q39, Q40, Q41, Q42, Q43, Q44, Q45]), "operationType" : NewBodyOperationType.INTERSECT, "oppositeDirection" : true, "depth" : 25 * mm, "offsetDistance" : 25 * mm});
        }
    });
